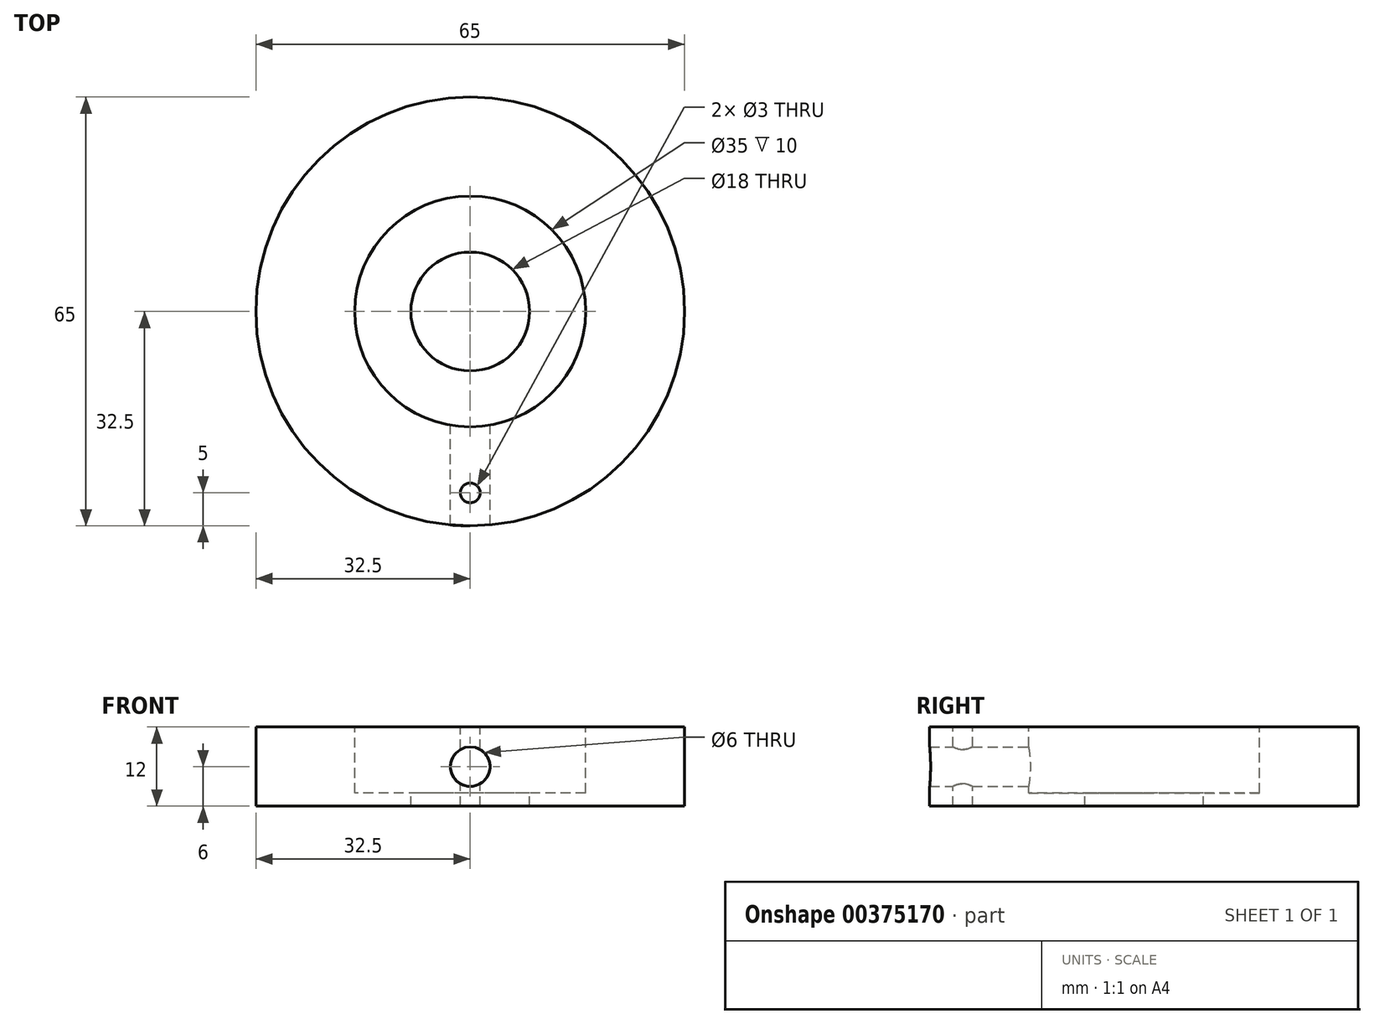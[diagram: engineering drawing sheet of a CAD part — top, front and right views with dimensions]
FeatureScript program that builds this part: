
annotation { "Feature Type Name" : "Feature", "Feature Type Description" : "" }
export const myFeature = defineFeature(function(context is Context, id is Id, definition is map)
    precondition{}
    {
        {
            var Q0;
            Q0=qCreatedBy(makeId("Top.planeOp"),FACE);
            var sketch = newSketch(context, id + "F0", { "sketchPlane" : qUnion([Q0])});
            skCircle(sketch, "E0", {"center": v(0, 0) * mm, "radius": 32.5 * mm});
            skSolve(sketch);
        }
        {
            var Q0;
            Q0=makeQuery(id+"F0.imprint","IMPRINT",FACE,{"disambiguationData":[TD([[makeQuery(id+"F0.imprint","IMPRINT",EDGE,{"derivedFrom":sQuery(id+"F0.wireOp",EDGE,"E0")}),1.0]])]});
            extrude(context, id + "F1", {"entities" : qUnion([Q0]), "depth" : 12 * mm});
        }
        {
            var Q0;
            Q0=makeQuery(id+"F1.opExtrude","CAP_FACE",FACE,{"disambiguationData":[OSD([sQuery(id+"F0.wireOp",EDGE,"E0")])],"isStart":false});
            var sketch = newSketch(context, id + "F2", { "sketchPlane" : qUnion([Q0])});
            skCircle(sketch, "E1", {"center": v(0, 0) * mm, "radius": 17.5 * mm});
            skSolve(sketch);
        }
        {
            var Q0;
            Q0=makeQuery(id+"F2.imprint","IMPRINT",FACE,{"disambiguationData":[TD([[makeQuery(id+"F2.imprint","IMPRINT",EDGE,{"derivedFrom":sQuery(id+"F2.wireOp",EDGE,"E1")}),1.0]])]});
            extrude(context, id + "F3", {"entities" : qUnion([Q0]), "operationType" : NewBodyOperationType.REMOVE, "oppositeDirection" : true, "depth" : 10 * mm});
        }
        {
            var Q0;
            Q0=makeQuery(id+"F3.boolean.opBoolean","COPY",FACE,{"derivedFrom":makeQuery(id+"F3.opExtrude","CAP_FACE",FACE,{"disambiguationData":[OSD([sQuery(id+"F2.wireOp",EDGE,"E1")])],"isStart":false})});
            var sketch = newSketch(context, id + "F4", { "sketchPlane" : qUnion([Q0])});
            skCircle(sketch, "E2", {"center": v(0, 0) * mm, "radius": 9 * mm});
            skSolve(sketch);
        }
        {
            var Q0;
            Q0=makeQuery(id+"F4.imprint","IMPRINT",FACE,{"disambiguationData":[TD([[makeQuery(id+"F4.imprint","IMPRINT",EDGE,{"derivedFrom":sQuery(id+"F4.wireOp",EDGE,"E2")}),1.0]])]});
            extrude(context, id + "F5", {"entities" : qUnion([Q0]), "operationType" : NewBodyOperationType.REMOVE, "oppositeDirection" : true, "depth" : 2000 * mm});
        }
        {
            var Q0;
            Q0=qCreatedBy(makeId("Front.planeOp"),FACE);
            var sketch = newSketch(context, id + "F6", { "sketchPlane" : qUnion([Q0])});
            skPoint(sketch, "E3", {"position": v(0, 6) * mm});
            skSolve(sketch);
        }
        {
            var Q0;
            Q0=sQuery(id+"F6.wireOp",VERTEX,"E3");
            var Q1;
            Q1=makeQuery(id+"F1.opExtrude","SWEPT_BODY",BODY,{"disambiguationData":[OSD([sQuery(id+"F0.wireOp",EDGE,"E0")])]});
            hole(context, id + "F7", {"style" : HoleStyle.SIMPLE, "endStyle" : HoleEndStyle.THROUGH, "oppositeDirection" : true, "holeDiameter" : 6 * mm, "isTappedThrough" : true, "tappedDepth" : 12 * mm, "tapClearance" : 3, "locations" : qUnion([Q0]), "scope" : qUnion([Q1])});
        }
        {
            var Q0;
            Q0=makeQuery(id+"F1.opExtrude","CAP_FACE",FACE,{"disambiguationData":[OSD([sQuery(id+"F0.wireOp",EDGE,"E0")])],"isStart":false});
            var sketch = newSketch(context, id + "F8", { "sketchPlane" : qUnion([Q0])});
            skPoint(sketch, "E4", {"position": v(0, -27.5) * mm});
            skSolve(sketch);
        }
        {
            var Q0;
            Q0=sQuery(id+"F8.wireOp",VERTEX,"E4");
            var Q1;
            Q1=makeQuery(id+"F1.opExtrude","SWEPT_BODY",BODY,{"disambiguationData":[OSD([sQuery(id+"F0.wireOp",EDGE,"E0")])]});
            hole(context, id + "F9", {"style" : HoleStyle.SIMPLE, "endStyle" : HoleEndStyle.THROUGH, "holeDiameter" : 3 * mm, "isTappedThrough" : true, "tappedDepth" : 12 * mm, "tapClearance" : 3, "locations" : qUnion([Q0]), "scope" : qUnion([Q1])});
        }
    });
